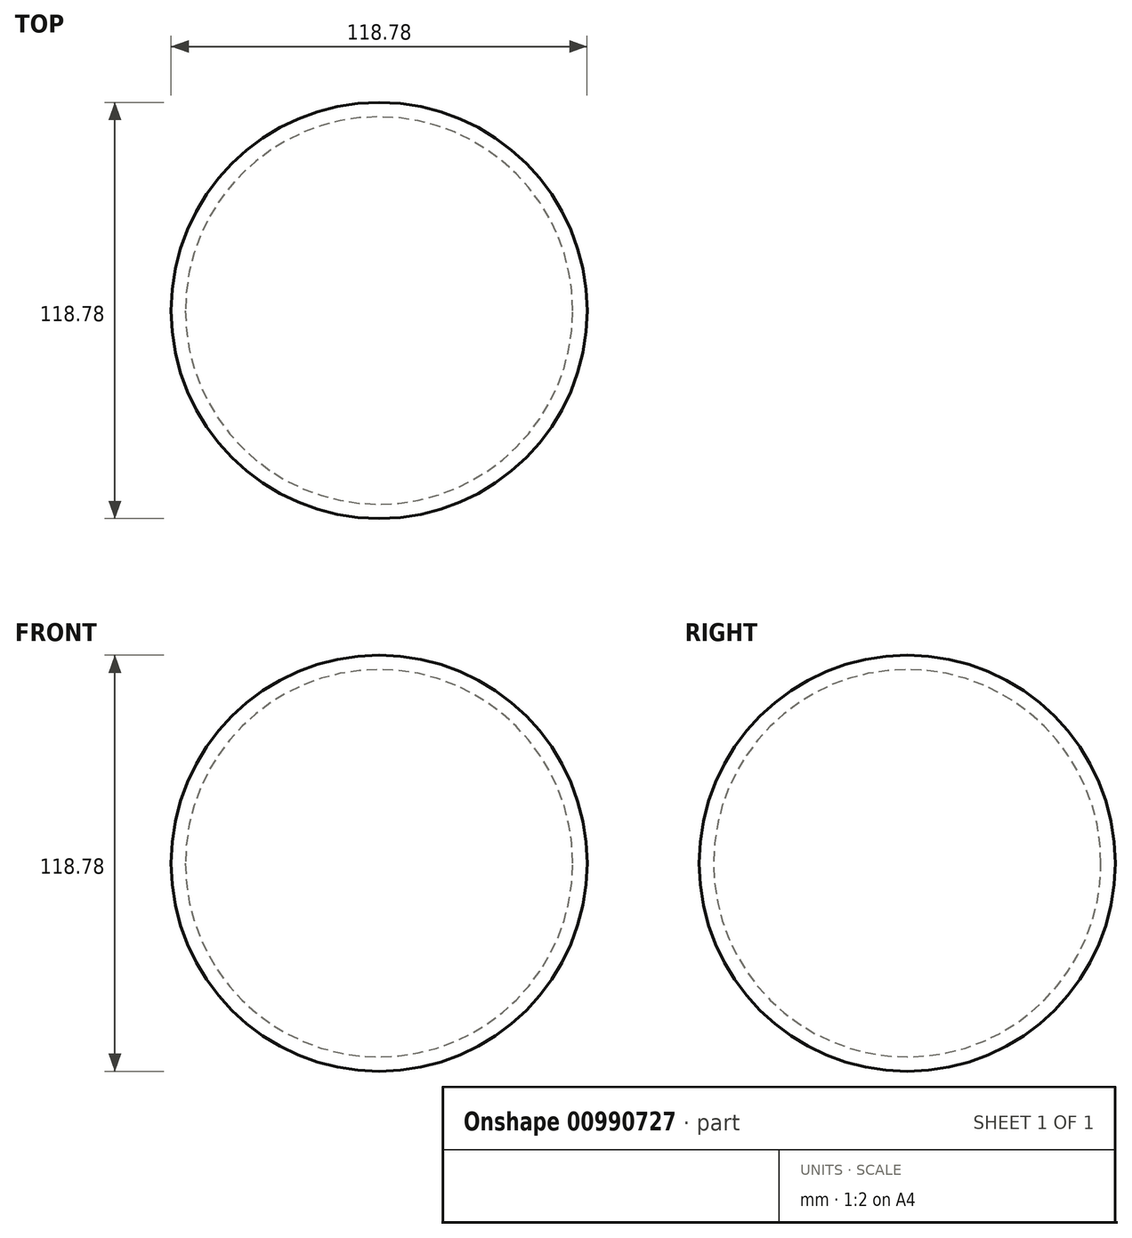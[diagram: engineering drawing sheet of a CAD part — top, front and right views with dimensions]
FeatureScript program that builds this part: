
annotation { "Feature Type Name" : "Feature", "Feature Type Description" : "" }
export const myFeature = defineFeature(function(context is Context, id is Id, definition is map)
    precondition{}
    {
        {
            var Q0;
            Q0=qCreatedBy(makeId("Top.planeOp"),FACE);
            var sketch = newSketch(context, id + "F0", { "sketchPlane" : qUnion([Q0])});
            skArc(sketch, "E0", {"start": v(55.3, 0) * mm, "mid": v(0, 55.3) * mm, "end": v(-55.3, 0) * mm});
            skArc(sketch, "E1", {"start": v(59.4, 0) * mm, "mid": v(0, 59.4) * mm, "end": v(-59.4, 0) * mm});
            skLineSegment(sketch, "E2", {"start": v(-59.4, 0) * mm, "end": v(-55.3, 0) * mm});
            skLineSegment(sketch, "E3.trimOffspring", {"start": v(55.3, 0) * mm, "end": v(59.4, 0) * mm});
            skPoint(sketch, "E4.orphan", {"position": v(-65.1, 0) * mm});
            skSolve(sketch);
        }
        {
            var Q0;
            Q0=qCreatedBy(makeId("Top.planeOp"),FACE);
            var sketch = newSketch(context, id + "F1", { "sketchPlane" : qUnion([Q0])});
            skLineSegment(sketch, "E5", {"start": v(0, 0) * mm, "end": v(69.02, 0) * mm});
            skSolve(sketch);
        }
        {
            var Q0;
            Q0=makeQuery(id+"F0.imprint","IMPRINT",FACE,{"disambiguationData":[TD([[makeQuery(id+"F0.imprint","IMPRINT",EDGE,{"derivedFrom":sQuery(id+"F0.wireOp",EDGE,"E0")}),-1.0]])]});
            var Q1;
            Q1=sQuery(id+"F1.wireOp",EDGE,"E5");
            revolve(context, id + "F2", {"surfaceOperationType" : NewSurfaceOperationType.NEW, "entities" : qUnion([Q0]), "axis" : qUnion([Q1]), "revolveType" : RevolveType.FULL});
        }
    });
